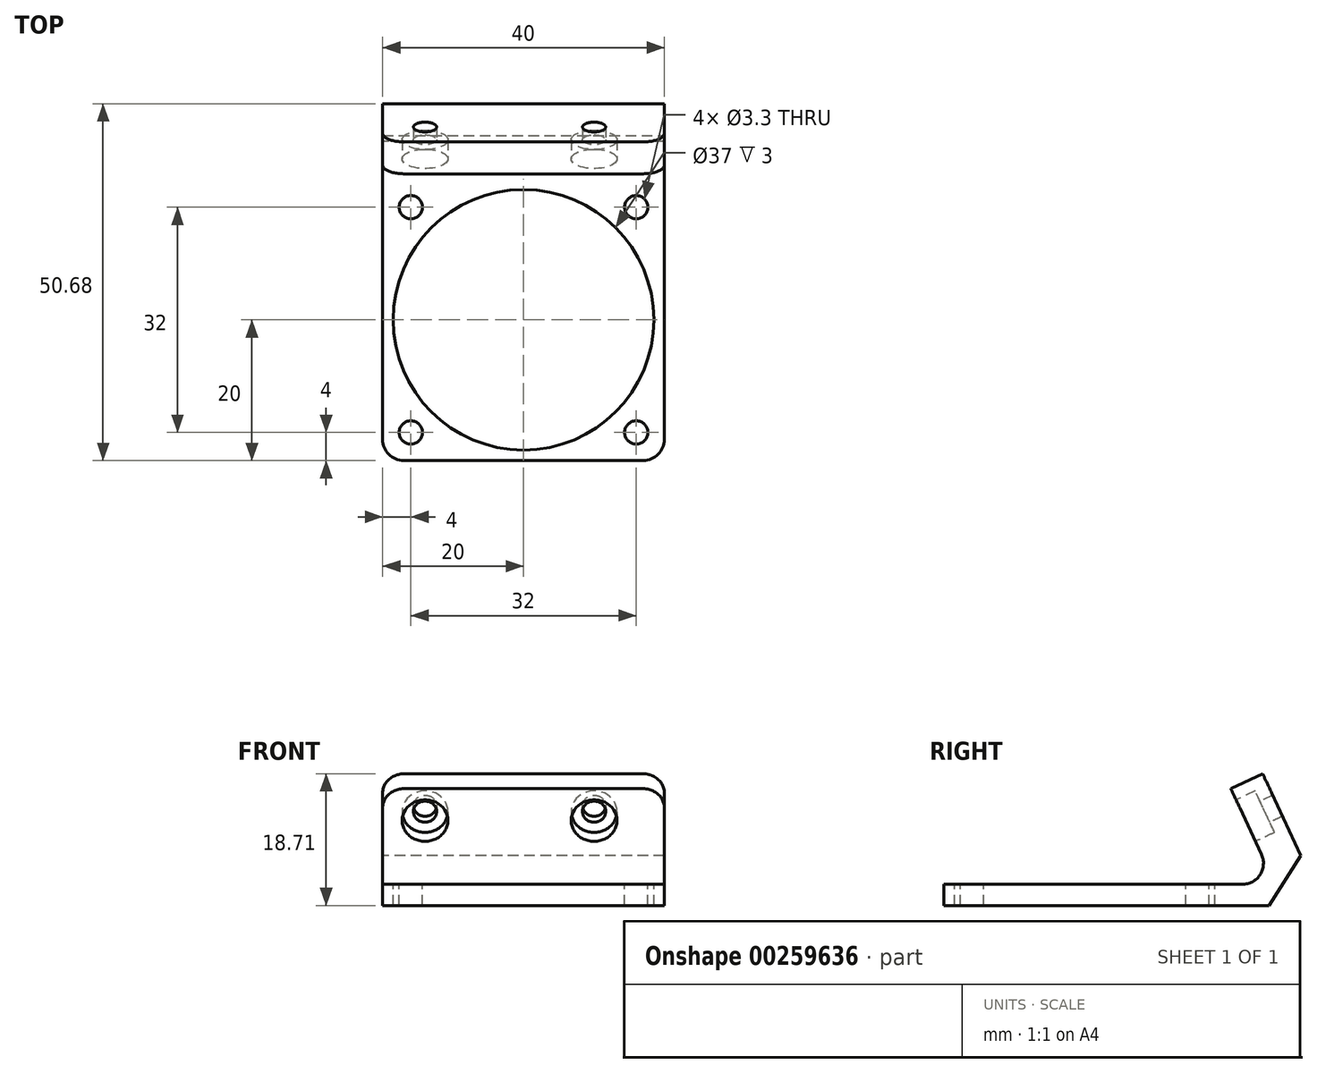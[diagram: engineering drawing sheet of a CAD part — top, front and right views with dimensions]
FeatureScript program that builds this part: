
annotation { "Feature Type Name" : "Feature", "Feature Type Description" : "" }
export const myFeature = defineFeature(function(context is Context, id is Id, definition is map)
    precondition{}
    {
        {
            var Q0;
            Q0=qCreatedBy(makeId("Right.planeOp"),FACE);
            var sketch = newSketch(context, id + "F0", { "sketchPlane" : qUnion([Q0])});
            skLineSegment(sketch, "E0", {"start": v(0, 0) * mm, "end": v(-54, 0) * mm});
            skLineSegment(sketch, "E1", {"start": v(-54, 0) * mm, "end": v(-54, 3) * mm});
            skLineSegment(sketch, "E2", {"start": v(-54, 3) * mm, "end": v(-11.62, 3) * mm});
            skLineSegment(sketch, "E3", {"start": v(-8.9, 7.27) * mm, "end": v(-13.26, 16.6) * mm});
            skLineSegment(sketch, "E4", {"start": v(-13.26, 16.6) * mm, "end": v(-8.72, 18.7) * mm});
            skLineSegment(sketch, "E5", {"start": v(-8.72, 18.7) * mm, "end": v(0, 0) * mm});
            skPoint(sketch, "E6.visualSharp", {"position": v(-6.92, 3) * mm});
            skArc(sketch, "E6.filletArc", {"start": v(-11.62, 3) * mm, "mid": v(-9.1, 4.39) * mm, "end": v(-8.9, 7.27) * mm});
            skSolve(sketch);
        }
        {
            var Q0;
            Q0 = qSketchRegion(id + "F0", true);
            extrude(context, id + "F1", {"entities" : qUnion([Q0]), "depth" : 40 * mm});
        }
        {
            var Q0;
            Q0=makeQuery(id+"F1.opExtrude","SWEPT_FACE",FACE,{"disambiguationData":[OSD([sQuery(id+"F0.wireOp",EDGE,"E2")])]});
            var sketch = newSketch(context, id + "F2", { "sketchPlane" : qUnion([Q0])});
            skLineSegment(sketch, "E7", {"start": v(0, -14) * mm, "end": v(40, -14) * mm, "construction": true});
            skLineSegment(sketch, "E8", {"start": v(0, -14) * mm, "end": v(40, -54) * mm, "construction": true});
            skLineSegment(sketch, "E9", {"start": v(0, -54) * mm, "end": v(40, -14) * mm, "construction": true});
            skLineSegment(sketch, "E10", {"start": v(20, -14) * mm, "end": v(20, -54) * mm, "construction": true});
            skCircle(sketch, "E11", {"center": v(20, -34) * mm, "radius": 18.5 * mm});
            skCircle(sketch, "E12", {"center": v(36, -18) * mm, "radius": 1.65 * mm});
            skCircle(sketch, "E13", {"center": v(4, -18) * mm, "radius": 1.65 * mm});
            skCircle(sketch, "E14", {"center": v(4, -50) * mm, "radius": 1.65 * mm});
            skCircle(sketch, "E15", {"center": v(36, -50) * mm, "radius": 1.65 * mm});
            skSolve(sketch);
        }
        {
            var Q0;
            Q0 = qSketchRegion(id + "F2", true);
            extrude(context, id + "F3", {"entities" : qUnion([Q0]), "operationType" : NewBodyOperationType.REMOVE, "endBound" : BoundingType.THROUGH_ALL, "oppositeDirection" : true, "depth" : 25 * mm});
        }
        {
            var Q0;
            Q0=makeQuery(id+"F1.opExtrude","CAP_EDGE",EDGE,{"disambiguationData":[OSD([sQuery(id+"F0.wireOp",EDGE,"E1")])],"isStart":true});
            var Q1;
            Q1=makeQuery(id+"F1.opExtrude","CAP_EDGE",EDGE,{"disambiguationData":[OSD([sQuery(id+"F0.wireOp",EDGE,"E1")])],"isStart":false});
            var Q2;
            Q2=makeQuery(id+"F1.opExtrude","CAP_EDGE",EDGE,{"disambiguationData":[OSD([sQuery(id+"F0.wireOp",EDGE,"E4")])],"isStart":true});
            var Q3;
            Q3=makeQuery(id+"F1.opExtrude","CAP_EDGE",EDGE,{"disambiguationData":[OSD([sQuery(id+"F0.wireOp",EDGE,"E4")])],"isStart":false});
            fillet(context, id + "F4", {"entities" : qUnion([Q0, Q1, Q2, Q3]), "radius" : 3 * mm, "tangentPropagation" : true, "allowEdgeOverflow" : false});
        }
        {
            var Q0;
            Q0=makeQuery(id+"F1.opExtrude","SWEPT_EDGE",EDGE,{"disambiguationData":[OSD([sQuery(id+"F0.wireOp",EDGE,"E0"),sQuery(id+"F0.wireOp",EDGE,"E5")])]});
            chamfer(context, id + "F5", {"entities" : qUnion([Q0]), "width" : 5 * mm, "tangentPropagation" : true});
        }
        {
            var Q0;
            Q0=makeQuery(id+"F1.opExtrude","SWEPT_FACE",FACE,{"disambiguationData":[OSD([sQuery(id+"F0.wireOp",EDGE,"E3")])]});
            var sketch = newSketch(context, id + "F6", { "sketchPlane" : qUnion([Q0])});
            skLineSegment(sketch, "E16", {"start": v(0, 15.64) * mm, "end": v(40, 15.64) * mm, "construction": true});
            skPoint(sketch, "E17", {"position": v(30.02, 15.64) * mm});
            skLineSegment(sketch, "E18", {"start": v(20, 15.64) * mm, "end": v(20, 20.64) * mm, "construction": true});
            skPoint(sketch, "E19", {"position": v(6.02, 15.64) * mm});
            skSolve(sketch);
        }
        {
            var Q0;
            Q0=sQuery(id+"F6.wireOp",VERTEX,"E19");
            var Q1;
            Q1=sQuery(id+"F6.wireOp",VERTEX,"E17");
            var Q2;
            Q2=makeQuery(id+"F1.opExtrude","SWEPT_BODY",BODY,{"disambiguationData":[OSD([sQuery(id+"F0.wireOp",EDGE,"E0"),sQuery(id+"F0.wireOp",EDGE,"E1"),sQuery(id+"F0.wireOp",EDGE,"E2"),sQuery(id+"F0.wireOp",EDGE,"E3"),sQuery(id+"F0.wireOp",EDGE,"E4"),sQuery(id+"F0.wireOp",EDGE,"E5"),sQuery(id+"F0.wireOp",EDGE,"E6.filletArc")])]});
            hole(context, id + "F7", {"style" : HoleStyle.C_BORE, "endStyle" : HoleEndStyle.THROUGH, "standardTappedOrClearance" : lookupTablePath({ "standard" : "ISO", "fit" : "Normal", "size" : "M3", "type" : "Clearance" }), "standardBlindInLast" : lookupTablePath({ "fit" : "Standard", "standard" : "ISO", "size" : "M3", "type" : "Clearance" }), "holeDiameter" : 3.3 * mm, "cBoreDiameter" : 6.5 * mm, "cBoreDepth" : 3 * mm, "tappedDepth" : 5.75 * mm, "tapClearance" : 3, "startFromSketch" : true, "locations" : qUnion([Q0, Q1]), "scope" : qUnion([Q2])});
        }
    });
